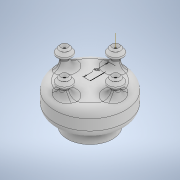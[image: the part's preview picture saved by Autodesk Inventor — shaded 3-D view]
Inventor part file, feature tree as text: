
AUTODESK INVENTOR PART (.ipt)
format: ipt  version: 2020 (Build 240168000, 168)  size: 531,968 bytes
history: native  units: in
note: dims shown in document units (in); Inventor stores cm internally (conversion verified against a paired STEP export)
features: sketch x3, revolve x2, fillet x2, other x1, pattern_circular x1
ambient origin geometry x8: Origin, YZ Plane, XZ Plane, XY Plane, X Axis, Y Axis, Z Axis, Center Point
bodies: Solid1 (feature_tree)
feature tree (9):
  revolve  "Revolution1"  [1 undecoded]
  sketch  "Sketch2"  dims[d2=0.2165in d3=0.0787in]
  other  "Work Axis1"
  revolve  "Revolution2"  [1 undecoded]
  pattern_circular  "Circular Pattern1"  [2 undecoded]
  fillet  "Fillet1"  Radius=0.1181in
  fillet  "Fillet2"  Radius=0.1181in
  sketch  "Sketch1"  dims[d0=0.1575in d1=0.2362in]
  sketch  "Sketch3"  dims[d4=0.1969in d5=0.1969in d6=0.1181in d7=0.1181in d9=90.0deg d10=0.4in d11=0.0197in d12=0.1181in d13=0.0in d14=0.0787in d15=135.0deg d16=0.0787in d17=0.0492in d18=0.0394in d20=90.0deg d26=90.0deg d27=1.5748in d28=360.0deg d30=0.0787in d31=0.125in d32=0.0197in]
note: 4 required parameter values undecoded (feature->parameter linkage not recoverable at this tier; creation-order binding heuristic only, values carry confidence <= 0.55)